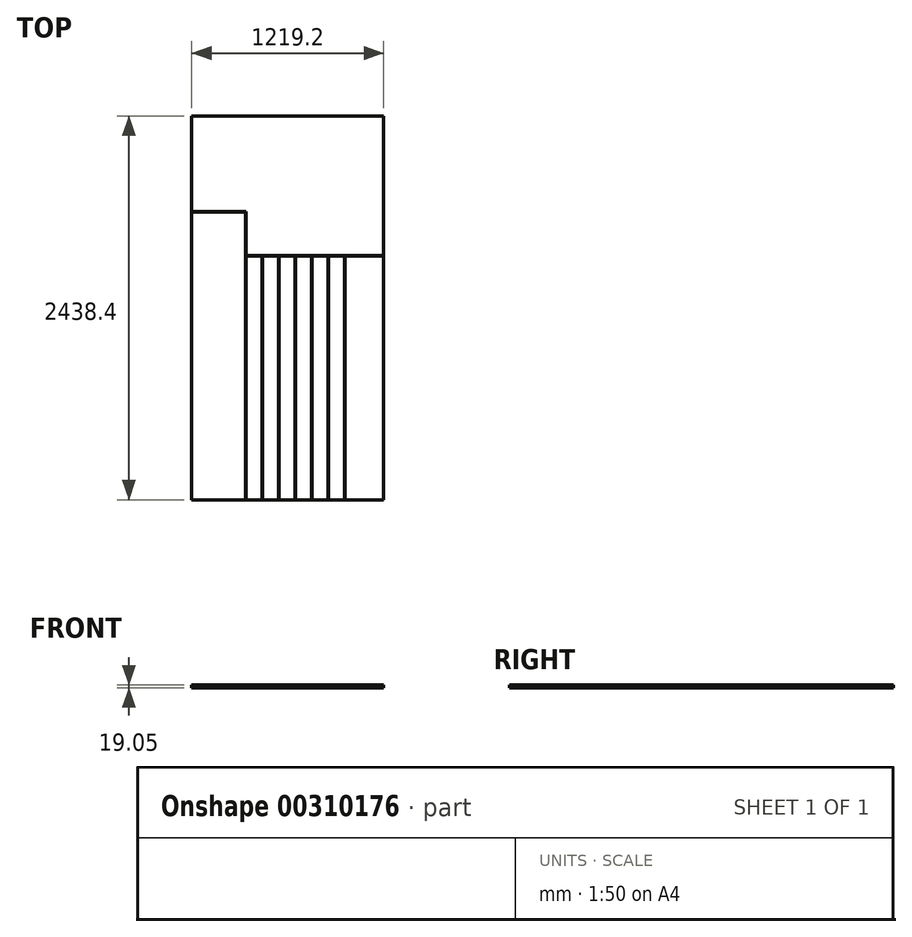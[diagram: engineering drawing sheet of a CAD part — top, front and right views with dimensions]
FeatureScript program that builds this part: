
annotation { "Feature Type Name" : "Feature", "Feature Type Description" : "" }
export const myFeature = defineFeature(function(context is Context, id is Id, definition is map)
    precondition{}
    {
        {
            var Q0;
            Q0=qCreatedBy(makeId("Top.planeOp"),FACE);
            var sketch = newSketch(context, id + "F0", { "sketchPlane" : qUnion([Q0])});
            skLineSegment(sketch, "E0.bottom", {"start": v(-609.6, -1219.2) * mm, "end": v(609.6, -1219.2) * mm});
            skLineSegment(sketch, "E0.top", {"start": v(-609.6, 1219.2) * mm, "end": v(609.6, 1219.2) * mm});
            skLineSegment(sketch, "E0.left", {"start": v(-609.6, -1219.2) * mm, "end": v(-609.6, 1219.2) * mm});
            skLineSegment(sketch, "E0.right", {"start": v(609.6, -1219.2) * mm, "end": v(609.6, 1219.2) * mm});
            skLineSegment(sketch, "E1", {"start": v(-609.6, 0) * mm, "end": v(609.6, 0) * mm, "construction": true});
            skLineSegment(sketch, "E2", {"start": v(0, -1219.2) * mm, "end": v(0, 1219.2) * mm, "construction": true});
            skSolve(sketch);
        }
        {
            var Q0;
            Q0 = qSketchRegion(id + "F0", true);
            extrude(context, id + "F1", {"entities" : qUnion([Q0]), "depth" : 19.05 * mm});
        }
        {
            var Q0;
            Q0=makeQuery(id+"F1.opExtrude","CAP_FACE",FACE,{"disambiguationData":[OSD([sQuery(id+"F0.wireOp",EDGE,"E0.bottom"),sQuery(id+"F0.wireOp",EDGE,"E0.top"),sQuery(id+"F0.wireOp",EDGE,"E0.left"),sQuery(id+"F0.wireOp",EDGE,"E0.right")])],"isStart":false});
            var sketch = newSketch(context, id + "F2", { "sketchPlane" : qUnion([Q0])});
            skLineSegment(sketch, "E3.bottom", {"start": v(-266.7, -1219.2) * mm, "end": v(-263.53, -1219.2) * mm});
            skLineSegment(sketch, "E3.top", {"start": v(-266.7, 609.6) * mm, "end": v(-263.53, 609.6) * mm});
            skLineSegment(sketch, "E3.left", {"start": v(-266.7, -1219.2) * mm, "end": v(-266.7, 609.6) * mm});
            skLineSegment(sketch, "E3.right", {"start": v(-263.53, -1219.2) * mm, "end": v(-263.53, 609.6) * mm});
            skLineSegment(sketch, "E4.bottom", {"start": v(-609.6, 612.78) * mm, "end": v(-263.52, 612.78) * mm});
            skLineSegment(sketch, "E4.top", {"start": v(-609.6, 609.6) * mm, "end": v(-263.53, 609.6) * mm});
            skLineSegment(sketch, "E4.left", {"start": v(-609.6, 612.78) * mm, "end": v(-609.6, 609.6) * mm});
            skLineSegment(sketch, "E4.right", {"start": v(-263.53, 612.78) * mm, "end": v(-263.53, 609.6) * mm});
            skLineSegment(sketch, "E5.bottom", {"start": v(-263.52, 330.2) * mm, "end": v(609.6, 330.2) * mm});
            skLineSegment(sketch, "E5.top", {"start": v(-263.52, 333.37) * mm, "end": v(609.6, 333.37) * mm});
            skLineSegment(sketch, "E5.left", {"start": v(-263.53, 330.2) * mm, "end": v(-263.53, 333.37) * mm});
            skLineSegment(sketch, "E5.right", {"start": v(609.6, 330.2) * mm, "end": v(609.6, 333.37) * mm});
            skLineSegment(sketch, "E6.bottom", {"start": v(-161.93, 330.2) * mm, "end": v(-158.75, 330.2) * mm});
            skLineSegment(sketch, "E6.top", {"start": v(-161.92, -1219.2) * mm, "end": v(-158.75, -1219.2) * mm});
            skLineSegment(sketch, "E6.left", {"start": v(-161.93, 330.2) * mm, "end": v(-161.92, -1219.2) * mm});
            skLineSegment(sketch, "E6.right", {"start": v(-158.75, 330.2) * mm, "end": v(-158.75, -1219.2) * mm});
            skLineSegment(sketch, "E7.bottom", {"start": v(-57.15, 330.2) * mm, "end": v(-53.97, 330.2) * mm});
            skLineSegment(sketch, "E7.top", {"start": v(-57.15, -1219.2) * mm, "end": v(-53.97, -1219.2) * mm});
            skLineSegment(sketch, "E7.left", {"start": v(-57.15, 330.2) * mm, "end": v(-57.15, -1219.2) * mm});
            skLineSegment(sketch, "E7.right", {"start": v(-53.97, 330.2) * mm, "end": v(-53.97, -1219.2) * mm});
            skLineSegment(sketch, "E8.bottom", {"start": v(47.63, 330.2) * mm, "end": v(50.8, 330.2) * mm});
            skLineSegment(sketch, "E8.top", {"start": v(47.63, -1219.2) * mm, "end": v(50.8, -1219.2) * mm});
            skLineSegment(sketch, "E8.left", {"start": v(47.63, 330.2) * mm, "end": v(47.63, -1219.2) * mm});
            skLineSegment(sketch, "E8.right", {"start": v(50.8, 330.2) * mm, "end": v(50.8, -1219.2) * mm});
            skLineSegment(sketch, "E9.bottom", {"start": v(152.4, 330.2) * mm, "end": v(155.58, 330.2) * mm});
            skLineSegment(sketch, "E9.top", {"start": v(152.4, -1219.2) * mm, "end": v(155.58, -1219.2) * mm});
            skLineSegment(sketch, "E9.left", {"start": v(152.4, 330.2) * mm, "end": v(152.4, -1219.2) * mm});
            skLineSegment(sketch, "E9.right", {"start": v(155.58, 330.2) * mm, "end": v(155.58, -1219.2) * mm});
            skLineSegment(sketch, "E10.bottom", {"start": v(257.18, 330.2) * mm, "end": v(260.35, 330.2) * mm});
            skLineSegment(sketch, "E10.top", {"start": v(257.18, -1219.2) * mm, "end": v(260.35, -1219.2) * mm});
            skLineSegment(sketch, "E10.left", {"start": v(257.18, 330.2) * mm, "end": v(257.18, -1219.2) * mm});
            skLineSegment(sketch, "E10.right", {"start": v(260.35, 330.2) * mm, "end": v(260.35, -1219.2) * mm});
            skLineSegment(sketch, "E11.bottom", {"start": v(361.95, 330.2) * mm, "end": v(365.13, 330.2) * mm});
            skLineSegment(sketch, "E11.top", {"start": v(361.95, -1219.2) * mm, "end": v(365.13, -1219.2) * mm});
            skLineSegment(sketch, "E11.left", {"start": v(361.95, 330.2) * mm, "end": v(361.95, -1219.2) * mm});
            skLineSegment(sketch, "E11.right", {"start": v(365.13, 330.2) * mm, "end": v(365.13, -1219.2) * mm});
            skLineSegment(sketch, "E12", {"start": v(-158.75, -1219.2) * mm, "end": v(-57.15, -1219.2) * mm, "construction": true});
            skLineSegment(sketch, "E13", {"start": v(-53.97, -1219.2) * mm, "end": v(47.63, -1219.2) * mm, "construction": true});
            skLineSegment(sketch, "E14", {"start": v(50.8, -1219.2) * mm, "end": v(152.4, -1219.2) * mm, "construction": true});
            skLineSegment(sketch, "E15", {"start": v(155.58, -1219.2) * mm, "end": v(257.18, -1219.2) * mm, "construction": true});
            skLineSegment(sketch, "E16", {"start": v(260.35, -1219.2) * mm, "end": v(361.95, -1219.2) * mm, "construction": true});
            skLineSegment(sketch, "E17", {"start": v(-263.53, -1219.2) * mm, "end": v(-161.92, -1219.2) * mm, "construction": true});
            skSolve(sketch);
        }
        {
            var Q0;
            Q0 = qSketchRegion(id + "F2", true);
            extrude(context, id + "F3", {"entities" : qUnion([Q0]), "operationType" : NewBodyOperationType.REMOVE, "endBound" : BoundingType.UP_TO_NEXT, "oppositeDirection" : true, "depth" : 25.4 * mm});
        }
    });
